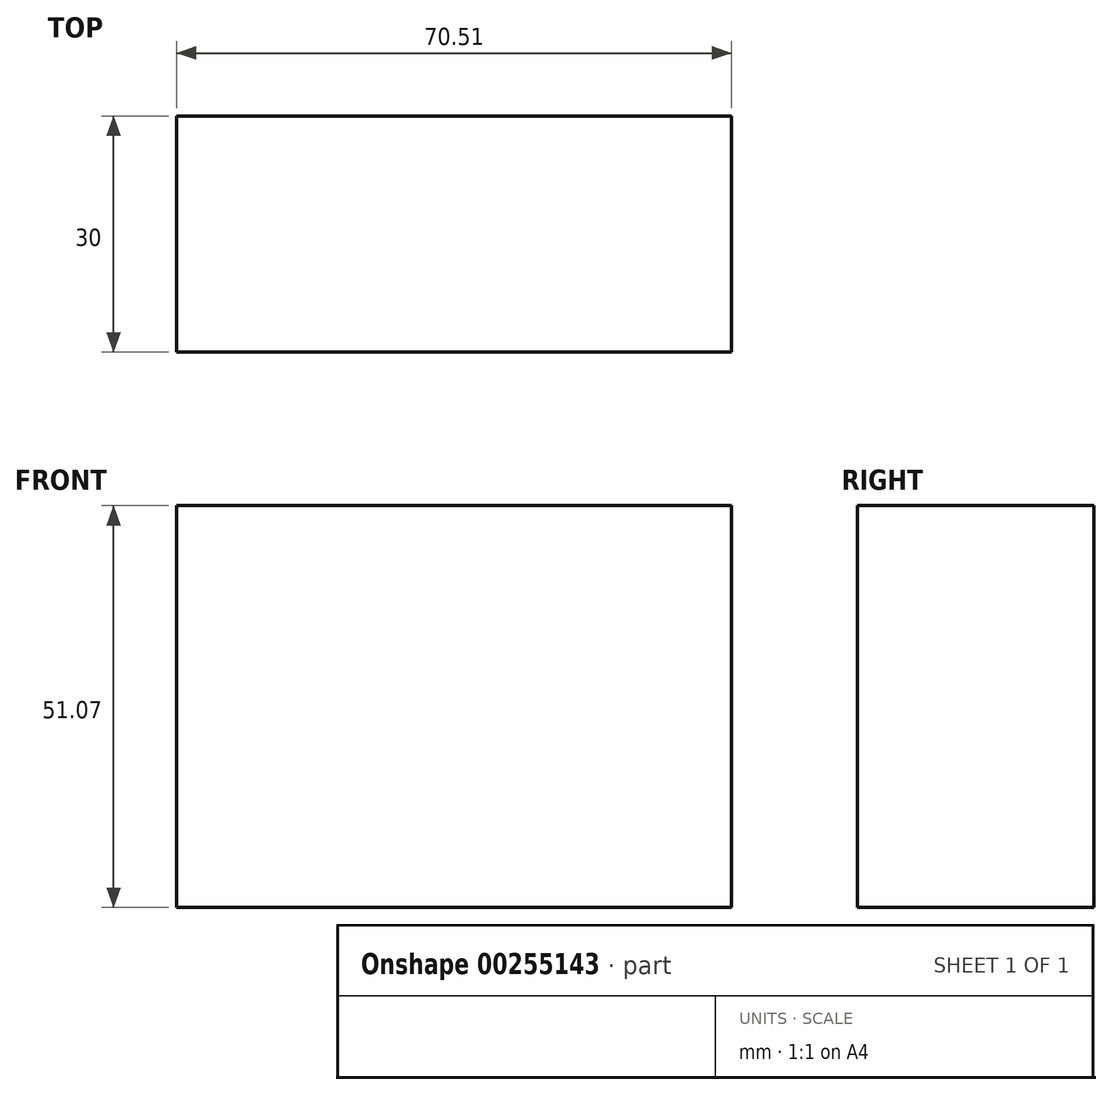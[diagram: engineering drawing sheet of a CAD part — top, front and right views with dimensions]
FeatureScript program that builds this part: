
annotation { "Feature Type Name" : "Feature", "Feature Type Description" : "" }
export const myFeature = defineFeature(function(context is Context, id is Id, definition is map)
    precondition{}
    {
        {
            var Q0;
            Q0=qCreatedBy(makeId("Front.planeOp"),FACE);
            var sketch = newSketch(context, id + "F0", { "sketchPlane" : qUnion([Q0])});
            skLineSegment(sketch, "E0.bottom", {"start": v(0, 0) * mm, "end": v(70.51, 0) * mm});
            skLineSegment(sketch, "E0.top", {"start": v(0, -51.07) * mm, "end": v(70.51, -51.07) * mm});
            skLineSegment(sketch, "E0.left", {"start": v(0, 0) * mm, "end": v(0, -51.07) * mm});
            skLineSegment(sketch, "E0.right", {"start": v(70.51, 0) * mm, "end": v(70.51, -51.07) * mm});
            skSolve(sketch);
        }
        {
            var Q0;
            Q0 = qSketchRegion(id + "F0", true);
            extrude(context, id + "F1", {"entities" : qUnion([Q0]), "depth" : 30 * mm});
        }
    });
